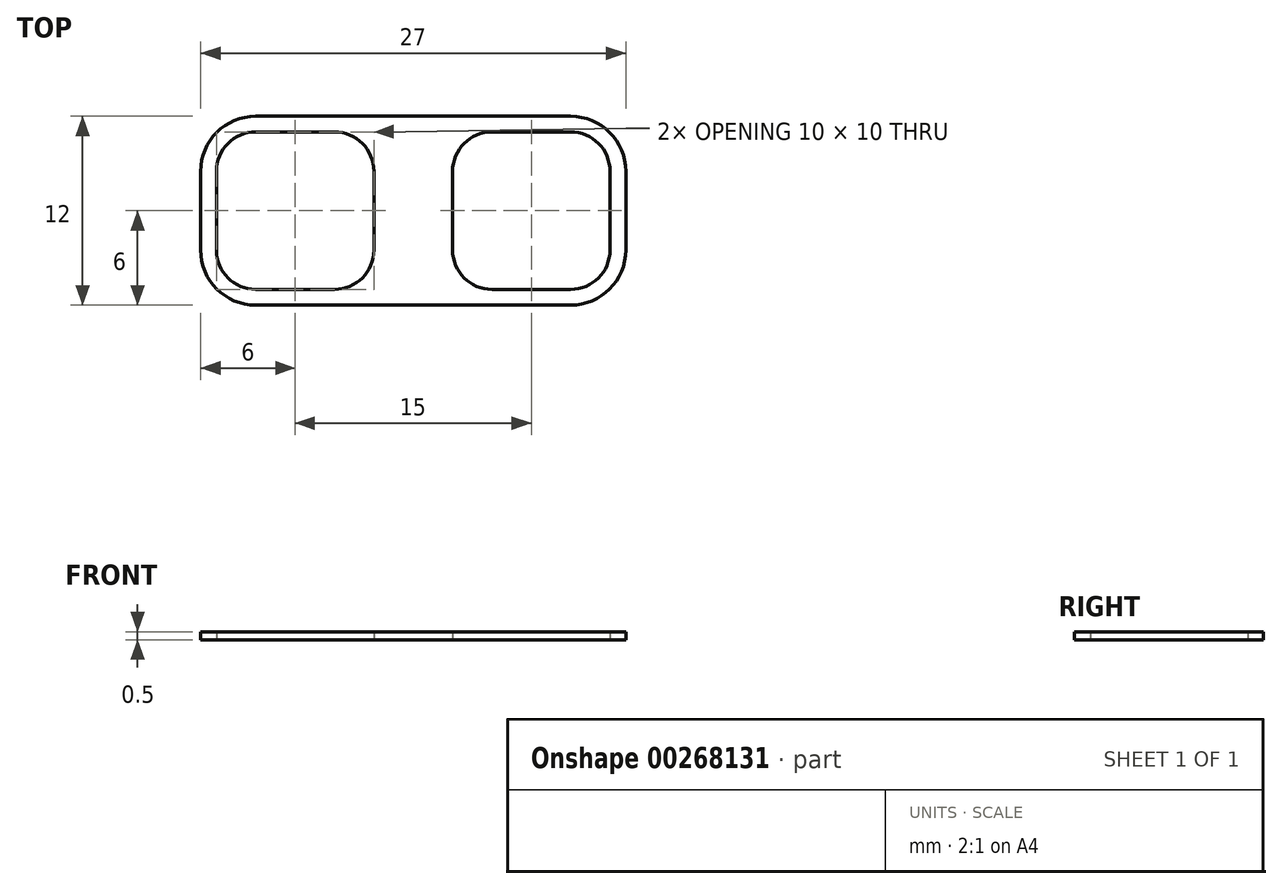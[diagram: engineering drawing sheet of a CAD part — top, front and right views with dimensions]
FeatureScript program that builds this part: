
annotation { "Feature Type Name" : "Feature", "Feature Type Description" : "" }
export const myFeature = defineFeature(function(context is Context, id is Id, definition is map)
    precondition{}
    {
        {
            var Q0;
            Q0=qCreatedBy(makeId("Top.planeOp"),FACE);
            var sketch = newSketch(context, id + "F0", { "sketchPlane" : qUnion([Q0])});
            skLineSegment(sketch, "E0", {"start": v(0, 0) * mm, "end": v(-7.5, 0) * mm});
            skLineSegment(sketch, "E1", {"start": v(0, 0) * mm, "end": v(7.5, 0) * mm});
            skLineSegment(sketch, "E2.bottom", {"start": v(-10, 5) * mm, "end": v(-5, 5) * mm});
            skLineSegment(sketch, "E2.top", {"start": v(-10, -5) * mm, "end": v(-5, -5) * mm});
            skLineSegment(sketch, "E2.left", {"start": v(-12.5, 2.5) * mm, "end": v(-12.5, -2.5) * mm});
            skLineSegment(sketch, "E2.right", {"start": v(-2.5, 2.5) * mm, "end": v(-2.5, -2.5) * mm});
            skPoint(sketch, "E2.middle", {"position": v(-7.5, 0) * mm});
            skLineSegment(sketch, "E3.bottom", {"start": v(10, 5) * mm, "end": v(5, 5) * mm});
            skLineSegment(sketch, "E3.top", {"start": v(10, -5) * mm, "end": v(5, -5) * mm});
            skLineSegment(sketch, "E3.left", {"start": v(12.5, 2.5) * mm, "end": v(12.5, -2.5) * mm});
            skLineSegment(sketch, "E3.right", {"start": v(2.5, 2.5) * mm, "end": v(2.5, -2.5) * mm});
            skPoint(sketch, "E3.middle", {"position": v(7.5, 0) * mm});
            skLineSegment(sketch, "E4", {"start": v(-12.5, 0) * mm, "end": v(-13.5, 0) * mm});
            skLineSegment(sketch, "E5", {"start": v(-13.5, 0) * mm, "end": v(-13.5, 2.5) * mm});
            skLineSegment(sketch, "E6", {"start": v(-10, 6) * mm, "end": v(10, 6) * mm});
            skLineSegment(sketch, "E7", {"start": v(13.5, 2.5) * mm, "end": v(13.5, -2.5) * mm});
            skLineSegment(sketch, "E8", {"start": v(10, -6) * mm, "end": v(-10, -6) * mm});
            skLineSegment(sketch, "E9", {"start": v(-13.5, -2.5) * mm, "end": v(-13.5, 0) * mm});
            skPoint(sketch, "E10.visualSharp", {"position": v(-12.5, 5) * mm});
            skArc(sketch, "E10.filletArc", {"start": v(-10, 5) * mm, "mid": v(-11.77, 4.27) * mm, "end": v(-12.5, 2.5) * mm});
            skPoint(sketch, "E11.visualSharp", {"position": v(-2.5, 5) * mm});
            skArc(sketch, "E11.filletArc", {"start": v(-2.5, 2.5) * mm, "mid": v(-3.23, 4.27) * mm, "end": v(-5, 5) * mm});
            skPoint(sketch, "E12.visualSharp", {"position": v(-2.5, -5) * mm});
            skArc(sketch, "E12.filletArc", {"start": v(-5, -5) * mm, "mid": v(-3.23, -4.27) * mm, "end": v(-2.5, -2.5) * mm});
            skPoint(sketch, "E13.visualSharp", {"position": v(-12.5, -5) * mm});
            skArc(sketch, "E13.filletArc", {"start": v(-12.5, -2.5) * mm, "mid": v(-11.77, -4.27) * mm, "end": v(-10, -5) * mm});
            skPoint(sketch, "E14.visualSharp", {"position": v(2.5, 5) * mm});
            skArc(sketch, "E14.filletArc", {"start": v(5, 5) * mm, "mid": v(3.23, 4.27) * mm, "end": v(2.5, 2.5) * mm});
            skPoint(sketch, "E15.visualSharp", {"position": v(12.5, 5) * mm});
            skArc(sketch, "E15.filletArc", {"start": v(12.5, 2.5) * mm, "mid": v(11.77, 4.27) * mm, "end": v(10, 5) * mm});
            skPoint(sketch, "E16.visualSharp", {"position": v(12.5, -5) * mm});
            skArc(sketch, "E16.filletArc", {"start": v(10, -5) * mm, "mid": v(11.77, -4.27) * mm, "end": v(12.5, -2.5) * mm});
            skPoint(sketch, "E17.visualSharp", {"position": v(2.5, -5) * mm});
            skArc(sketch, "E17.filletArc", {"start": v(2.5, -2.5) * mm, "mid": v(3.23, -4.27) * mm, "end": v(5, -5) * mm});
            skPoint(sketch, "E18.visualSharp", {"position": v(-13.5, 6) * mm});
            skArc(sketch, "E18.filletArc", {"start": v(-10, 6) * mm, "mid": v(-12.47, 4.97) * mm, "end": v(-13.5, 2.5) * mm});
            skPoint(sketch, "E19.visualSharp", {"position": v(13.5, 6) * mm});
            skArc(sketch, "E19.filletArc", {"start": v(13.5, 2.5) * mm, "mid": v(12.47, 4.97) * mm, "end": v(10, 6) * mm});
            skPoint(sketch, "E20.visualSharp", {"position": v(13.5, -6) * mm});
            skArc(sketch, "E20.filletArc", {"start": v(10, -6) * mm, "mid": v(12.47, -4.97) * mm, "end": v(13.5, -2.5) * mm});
            skPoint(sketch, "E21.visualSharp", {"position": v(-13.5, -6) * mm});
            skArc(sketch, "E21.filletArc", {"start": v(-13.5, -2.5) * mm, "mid": v(-12.47, -4.97) * mm, "end": v(-10, -6) * mm});
            skSolve(sketch);
        }
        {
            var Q0;
            Q0=makeQuery(id+"F0.imprint","IMPRINT",FACE,{"disambiguationData":[TD([[makeQuery(id+"F0.imprint","IMPRINT",EDGE,{"derivedFrom":sQuery(id+"F0.wireOp",EDGE,"E2.bottom")}),1.0]])]});
            extrude(context, id + "F1", {"entities" : qUnion([Q0]), "depth" : 0.5 * mm, "offsetDistance" : 25 * mm});
        }
    });
